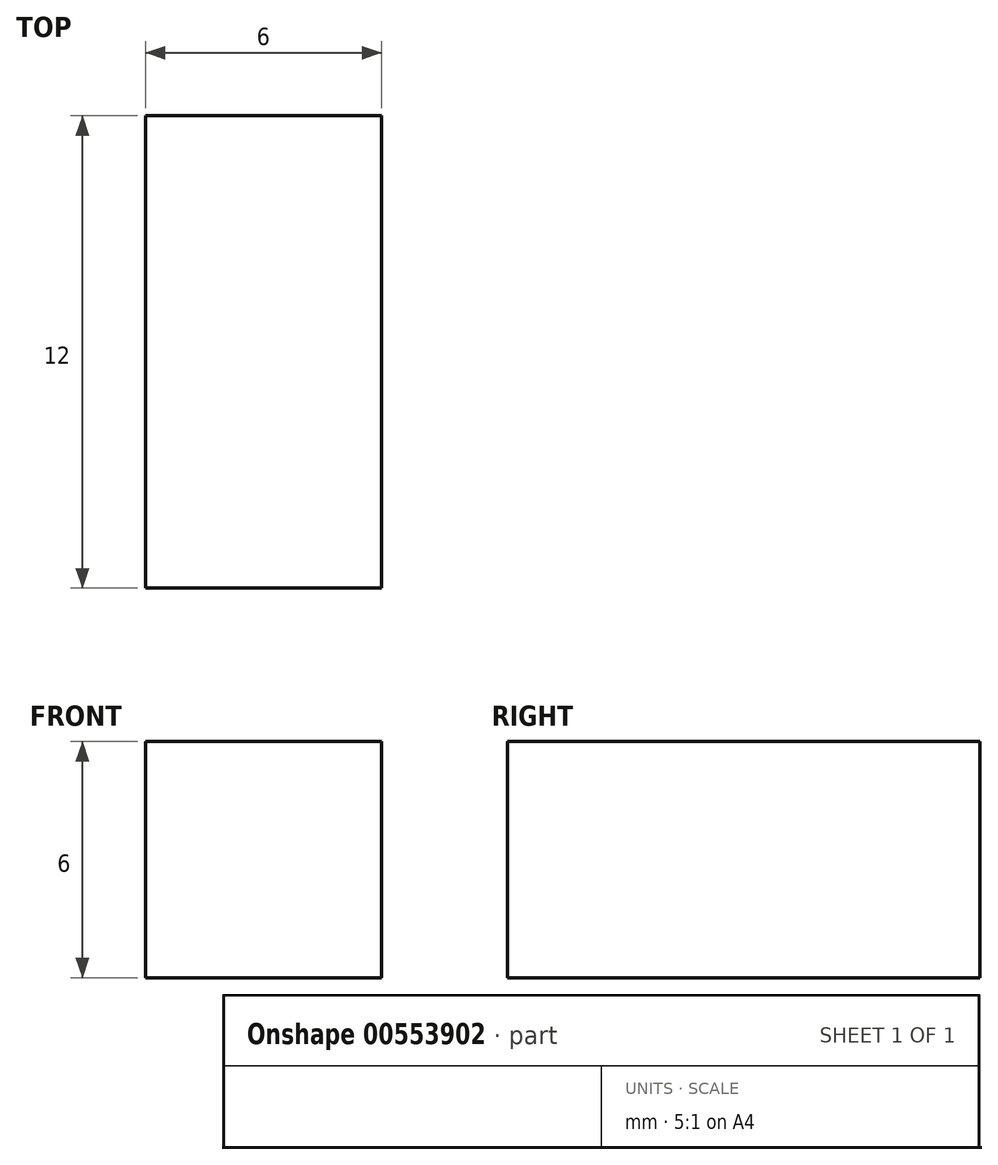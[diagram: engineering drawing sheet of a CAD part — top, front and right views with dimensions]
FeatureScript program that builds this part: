
annotation { "Feature Type Name" : "Feature", "Feature Type Description" : "" }
export const myFeature = defineFeature(function(context is Context, id is Id, definition is map)
    precondition{}
    {
        {
            var Q0;
            Q0=qCreatedBy(makeId("Front.planeOp"),FACE);
            var sketch = newSketch(context, id + "F0", { "sketchPlane" : qUnion([Q0])});
            skLineSegment(sketch, "E0.bottom", {"start": v(-3, 0) * mm, "end": v(3, 0) * mm});
            skLineSegment(sketch, "E0.top", {"start": v(-3, 6) * mm, "end": v(3, 6) * mm});
            skLineSegment(sketch, "E0.left", {"start": v(-3, 0) * mm, "end": v(-3, 6) * mm});
            skLineSegment(sketch, "E0.right", {"start": v(3, 0) * mm, "end": v(3, 6) * mm});
            skSolve(sketch);
        }
        {
            var Q0;
            Q0=makeQuery(id+"F0.imprint","IMPRINT",FACE,{"disambiguationData":[TD([[makeQuery(id+"F0.imprint","IMPRINT",EDGE,{"derivedFrom":sQuery(id+"F0.wireOp",EDGE,"E0.bottom")}),1.0]])]});
            extrude(context, id + "F1", {"entities" : qUnion([Q0]), "depth" : 12 * mm, "offsetDistance" : 25 * mm});
        }
    });
